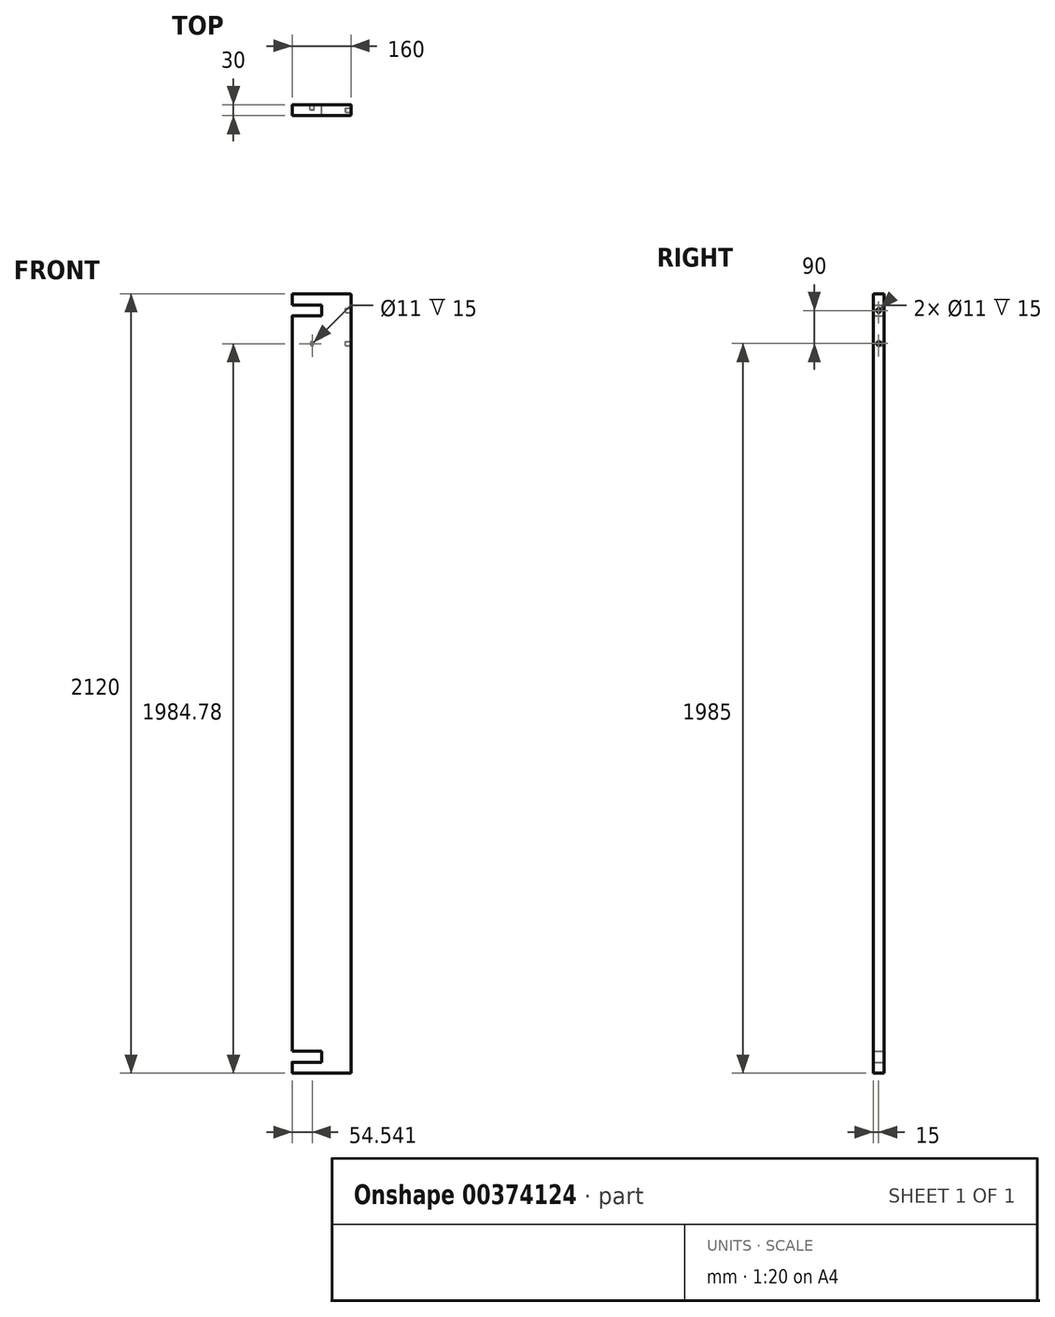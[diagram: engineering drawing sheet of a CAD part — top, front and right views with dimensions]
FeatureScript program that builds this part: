
annotation { "Feature Type Name" : "Feature", "Feature Type Description" : "" }
export const myFeature = defineFeature(function(context is Context, id is Id, definition is map)
    precondition{}
    {
        {
            var Q0;
            Q0=qCreatedBy(makeId("Top.planeOp"),FACE);
            var sketch = newSketch(context, id + "F0", { "sketchPlane" : qUnion([Q0])});
            skLineSegment(sketch, "E0.bottom", {"start": v(80, -15) * mm, "end": v(-80, -15) * mm});
            skLineSegment(sketch, "E0.top", {"start": v(80, 15) * mm, "end": v(-80, 15) * mm});
            skLineSegment(sketch, "E0.left", {"start": v(80, -15) * mm, "end": v(80, 15) * mm});
            skLineSegment(sketch, "E0.right", {"start": v(-80, -15) * mm, "end": v(-80, 15) * mm});
            skPoint(sketch, "E0.middle", {"position": v(0, 0) * mm});
            skSolve(sketch);
        }
        {
            var Q0;
            Q0 = qSketchRegion(id + "F0", true);
            extrude(context, id + "F1", {"entities" : qUnion([Q0]), "depth" : 2120 * mm, "symmetric" : true});
        }
        {
            var Q0;
            Q0=makeQuery(id+"F1.opExtrude","SWEPT_FACE",FACE,{"disambiguationData":[OSD([sQuery(id+"F0.wireOp",EDGE,"E0.bottom")])]});
            var Q1;
            Q1=makeQuery(id+"F1.opExtrude","SWEPT_FACE",FACE,{"disambiguationData":[OSD([sQuery(id+"F0.wireOp",EDGE,"E0.top")])]});
            var Q2;
            Q2=makeQuery(id+"F1.opExtrude","CAP_FACE",FACE,{"disambiguationData":[OSD([sQuery(id+"F0.wireOp",EDGE,"E0.bottom"),sQuery(id+"F0.wireOp",EDGE,"E0.top"),sQuery(id+"F0.wireOp",EDGE,"E0.left"),sQuery(id+"F0.wireOp",EDGE,"E0.right")])],"isStart":false});
            var Q3;
            Q3=makeQuery(id+"F1.opExtrude","SWEPT_FACE",FACE,{"disambiguationData":[OSD([sQuery(id+"F0.wireOp",EDGE,"E0.left")])]});
            var Q4;
            Q4=makeQuery(id+"F1.opExtrude","CAP_FACE",FACE,{"disambiguationData":[OSD([sQuery(id+"F0.wireOp",EDGE,"E0.bottom"),sQuery(id+"F0.wireOp",EDGE,"E0.top"),sQuery(id+"F0.wireOp",EDGE,"E0.left"),sQuery(id+"F0.wireOp",EDGE,"E0.right")])],"isStart":true});
            var Q5;
            Q5=makeQuery(id+"F1.opExtrude","SWEPT_FACE",FACE,{"disambiguationData":[OSD([sQuery(id+"F0.wireOp",EDGE,"E0.right")])]});
            fillet(context, id + "F2", {"entities" : qUnion([Q0, Q1, Q2, Q3, Q4, Q5]), "radius" : 2 * mm, "tangentPropagation" : true, "allowEdgeOverflow" : false});
        }
        {
            var Q0;
            Q0=makeQuery(id+"F1.opExtrude","SWEPT_FACE",FACE,{"disambiguationData":[OSD([sQuery(id+"F0.wireOp",EDGE,"E0.top")])]});
            var sketch = newSketch(context, id + "F3", { "sketchPlane" : qUnion([Q0])});
            skLineSegment(sketch, "E1.bottom", {"start": v(80, 1030) * mm, "end": v(0, 1030) * mm});
            skLineSegment(sketch, "E1.top", {"start": v(80, 1000) * mm, "end": v(0, 1000) * mm});
            skLineSegment(sketch, "E1.left", {"start": v(80, 1030) * mm, "end": v(80, 1000) * mm});
            skLineSegment(sketch, "E1.right", {"start": v(0, 1030) * mm, "end": v(0, 1000) * mm});
            skLineSegment(sketch, "E2.MirrorCS", {"start": v(0, -1030) * mm, "end": v(0, -1000) * mm});
            skLineSegment(sketch, "E3.MirrorCS", {"start": v(80, -1030) * mm, "end": v(80, -1000) * mm});
            skLineSegment(sketch, "E4.MirrorCS", {"start": v(80, -1030) * mm, "end": v(0, -1030) * mm});
            skLineSegment(sketch, "E5.MirrorCS", {"start": v(80, -1000) * mm, "end": v(0, -1000) * mm});
            skCircle(sketch, "E6", {"center": v(25.46, 924.78) * mm, "radius": 5.5 * mm});
            skSolve(sketch);
        }
        {
            var Q0;
            {var subQ0=sQuery(id+"F3.wireOp",EDGE,"E1.left");Q0=makeQuery(id+"F3.imprint","IMPRINT",FACE,{"disambiguationData":[TD([[makeQuery(id+"F3.imprint","IMPRINT",EDGE,{"derivedFrom":subQ0}),-1.0]])]});}
            var Q1;
            {var subQ0=sQuery(id+"F3.wireOp",EDGE,"E1.right");Q1=makeQuery(id+"F3.imprint","IMPRINT",FACE,{"disambiguationData":[TD([[makeQuery(id+"F3.imprint","IMPRINT",EDGE,{"derivedFrom":subQ0}),1.0]])]});}
            var Q2;
            {var subQ0=sQuery(id+"F3.wireOp",EDGE,"E3.MirrorCS");Q2=makeQuery(id+"F3.imprint","IMPRINT",FACE,{"disambiguationData":[TD([[makeQuery(id+"F3.imprint","IMPRINT",EDGE,{"derivedFrom":subQ0}),1.0]])]});}
            var Q3;
            {var subQ0=sQuery(id+"F3.wireOp",EDGE,"E2.MirrorCS");Q3=makeQuery(id+"F3.imprint","IMPRINT",FACE,{"disambiguationData":[TD([[makeQuery(id+"F3.imprint","IMPRINT",EDGE,{"derivedFrom":subQ0}),-1.0]])]});}
            extrude(context, id + "F4", {"entities" : qUnion([Q0, Q1, Q2, Q3]), "operationType" : NewBodyOperationType.REMOVE, "endBound" : BoundingType.THROUGH_ALL, "oppositeDirection" : true, "depth" : 25 * mm});
        }
        {
            var Q0;
            Q0 = qSketchRegion(id + "F3", true);
            extrude(context, id + "F5", {"entities" : qUnion([Q0]), "operationType" : NewBodyOperationType.REMOVE, "oppositeDirection" : true, "depth" : 15 * mm});
        }
        {
            var Q0;
            Q0=makeQuery(id+"F1.opExtrude","SWEPT_FACE",FACE,{"disambiguationData":[OSD([sQuery(id+"F0.wireOp",EDGE,"E0.left")])]});
            var sketch = newSketch(context, id + "F6", { "sketchPlane" : qUnion([Q0])});
            skCircle(sketch, "E7", {"center": v(0, 1015) * mm, "radius": 5.5 * mm});
            skPoint(sketch, "E7.centerSnap0", {"position": v(0, 1058) * mm});
            skCircle(sketch, "E8.0.1.0", {"center": v(0, 925) * mm, "radius": 5.5 * mm});
            skLineSegment(sketch, "E8.direction1", {"start": v(0, 1015) * mm, "end": v(25, 1015) * mm, "construction": true});
            skLineSegment(sketch, "E8.direction2", {"start": v(0, 1015) * mm, "end": v(0, 925) * mm, "construction": true});
            skLineSegment(sketch, "E9", {"start": v(-13, 0) * mm, "end": v(13, 0) * mm, "construction": true});
            skLineSegment(sketch, "E10.MirrorCS", {"start": v(13, 0) * mm, "end": v(-13, 0) * mm, "construction": true});
            skSolve(sketch);
        }
        {
            var Q0;
            Q0=makeQuery(id+"F6.imprint","IMPRINT",FACE,{"disambiguationData":[TD([[makeQuery(id+"F6.imprint","IMPRINT",EDGE,{"derivedFrom":sQuery(id+"F6.wireOp",EDGE,"E7")}),1.0]])]});
            var Q1;
            Q1=makeQuery(id+"F6.imprint","IMPRINT",FACE,{"disambiguationData":[TD([[makeQuery(id+"F6.imprint","IMPRINT",EDGE,{"derivedFrom":sQuery(id+"F6.wireOp",EDGE,"E8.0.1.0")}),1.0]])]});
            extrude(context, id + "F7", {"entities" : qUnion([Q0, Q1]), "operationType" : NewBodyOperationType.REMOVE, "oppositeDirection" : true, "depth" : 15 * mm});
        }
    });
